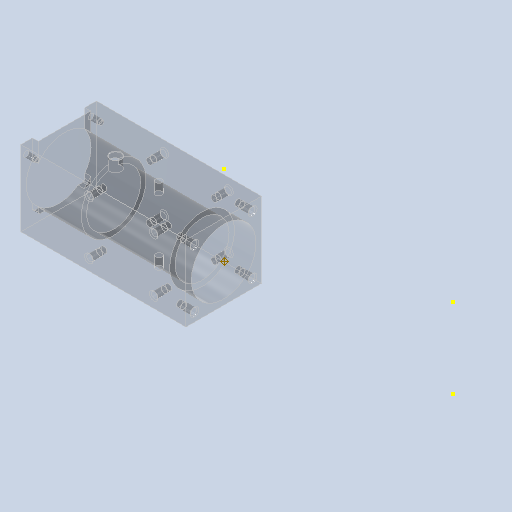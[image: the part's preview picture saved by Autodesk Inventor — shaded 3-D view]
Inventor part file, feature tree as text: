
AUTODESK INVENTOR PART (.ipt)
format: ipt  version: 2022 (Build 260153000, 153)  size: 289,792 bytes
history: native  units: mm
features: sketch x9, plane x4, extrude x4, chamfer x4, hole x3, projected_geometry x2, other x1, revolve x1, mirror x1
ambient origin geometry x8: Origin, YZ Plane, XZ Plane, XY Plane, X Axis, Y Axis, Z Axis, Center Point
bodies: Body1 (feature_tree)
feature tree (29):
  sketch  "Sketch1"  dims[d0=76.5mm d1=35.0mm]
  sketch  "Sketch3"  dims[d2=30.0mm d3=25.5mm]
  plane  "Work Plane1"
  sketch  "Sketch4"  dims[d4=10.0mm d5=25.0mm]
  other  "Work Point1"
  sketch  "Sketch5"  dims[d6=30.0mm d10=35.0mm]
  plane  "Work Plane2"
  extrude  "Extrusion1"  Depth=35.0mm
  revolve  "Revolution2"  [1 undecoded]
  hole  "Hole1"  [1 undecoded]
  sketch  "Sketch8"  dims[d14=90.0deg d21=38.18mm]
  extrude  "Extrusion2"  Depth=35.0mm
  hole  "Hole2"  [1 undecoded]
  plane  "Work Plane3"
  sketch  "Sketch9"  dims[d22=3.0mm d23=40.0mm d25=360.0deg]
  sketch  "Sketch11"  dims[d27=2.8mm d28=6.0mm d29=3.0mm d30=5.0mm d31=90.0deg d32=7.0mm d33=20.594885mm d34=2.5mm]
  extrude  "Extrusion3"  Depth=38.18mm
  extrude  "Extrusion4"  Depth=40.0mm TaperAngle=360.0deg
  hole  "Hole3"  [1 undecoded]
  plane  "Work Plane4"
  mirror  "Mirror2"
  chamfer  "Chamfer3"  Distance=5.0mm
  chamfer  "Chamfer4"  Distance=1.0mm
  chamfer  "Chamfer5"  Distance=29.5mm
  chamfer  "Chamfer6"  Distance=24.4mm
  sketch  "Sketch7"  dims[d11=35.0mm d12=10.0mm d13=0.0mm]
  projected_geometry  "Projected Loop1"
  sketch  "Sketch12"  dims[d35=2.5mm d36=5.0mm d38=1.0mm d39=29.5mm d40=24.4mm d41=2.75mm d42=0.0mm d43=2.0mm d44=6.0mm d45=2.5mm d46=4.0mm d47=90.0deg d48=5.0mm d49=20.594885mm d54=3.0mm d55=5.0mm d56=30.0mm d57=50.0mm d58=2.75mm d59=0.0mm d60=10.0mm d61=0.0mm d62=3.0mm d63=15.0mm d64=5.0mm d65=20.0mm d67=30.0mm d68=10.0mm d70=10.0mm d72=2.8mm d73=6.0mm d74=3.0mm d75=5.0mm d76=90.0deg d77=7.0mm d78=20.594885mm d85=0.5mm d86=2.0mm d87=45.0deg d88=0.5mm d89=2.0mm d90=45.0deg d91=0.5mm d92=2.0mm d93=45.0deg d94=0.2mm d95=2.0mm d96=45.0deg]
  projected_geometry  "Projected Loop2"
note: 4 required parameter values undecoded (feature->parameter linkage not recoverable at this tier; creation-order binding heuristic only, values carry confidence <= 0.55)